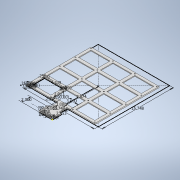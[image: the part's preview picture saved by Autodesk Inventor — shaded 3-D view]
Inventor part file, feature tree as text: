
AUTODESK INVENTOR PART (.ipt)
format: ipt  version: 2020 (Build 240168000, 168)  size: 301,056 bytes
history: native  units: in
note: dims shown in document units (in); Inventor stores cm internally (conversion verified against a paired STEP export)
features: extrude x4, sketch x3, hole x2, pattern_linear x1
ambient origin geometry x8: Origin, YZ Plane, XZ Plane, XY Plane, X Axis, Y Axis, Z Axis, Center Point
bodies: Solid1 (feature_tree)
feature tree (10):
  sketch  "Sketch1"  dims[d0=3.0in d1=2.0in]
  extrude  "Extrusion1"  Depth=2.0in
  hole  "Hole1"  [1 undecoded]
  sketch  "Sketch2"  dims[d2=0.25in d3=1.0in]
  extrude  "Extrusion2"  TaperAngle=0.0deg  [1 undecoded]
  hole  "Hole2"  [1 undecoded]
  extrude  "Extrusion3"  Depth=0.5in
  pattern_linear  "Rectangular Pattern1"  Spacing1=0.25in  [1 undecoded]
  extrude  "Extrusion4"  Depth=0.25in
  sketch  "Sketch3"  dims[d4=1.0in d5=0.0in d6=0.5in d7=0.5in d8=0.25in d9=0.25in d10=2.9528in d11=90.0deg d12=2.9528in d13=1.0in d14=7.874in d15=90.0deg d16=15.748in d17=15.748in d18=0.25in d19=0.0in d20=0.26in d21=0.5in d22=0.375in d23=0.25in d24=0.5635in d25=1.0in d26=0.8108in d27=0.25in d28=90.0deg d29=0.25in d30=0.25in d31=0.25in d32=4.3386in d33=2.9134in d34=0.25in d35=0.25in d36=0.25in d37=0.25in d38=0.25in d39=0.315in d40=90.0deg d41=0.0787in d42=0.0787in d43=0.0787in d44=0.0787in d45=0.0in d46=0.0in d47=0.203in d48=0.625in d49=0.375in d50=0.25in d51=0.5635in d52=1.0in d53=0.8108in d54=0.0787in d55=0.0in d56=1.1811in d58=4.839in d59=1.5748in d61=3.423in d62=0.25in d63=0.25in d64=0.0in d65=0.0in]
note: 4 required parameter values undecoded (feature->parameter linkage not recoverable at this tier; creation-order binding heuristic only, values carry confidence <= 0.55)
